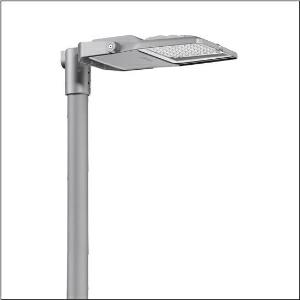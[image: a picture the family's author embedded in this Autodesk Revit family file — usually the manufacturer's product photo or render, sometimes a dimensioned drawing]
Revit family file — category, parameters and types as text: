
# Revit family: floodlight_fl_21_iq_mini___pl33t_5xa7772d2f3a_d038
name_source: partatom
category: Lighting Fixtures
units: mm (PartAtom-declared; Revit-internal decimal feet)

## family parameters
Cut with Voids When Loaded = No
Host = Face
Light Source = No
Part Type = Normal
Room Calculation Point = No
Round Connector Dimension = Use Diameter
Shared = No

## types (1)
- --- (1 x LED, 17620 lm, 143 W, 3000K)
    Apparent Load = 143 VA
    CIE Flux Codes = 26 75 99 100 100
    Color Rendering = 70
    Color Temperature = 3000K
    Default Elevation = 1800 mm
    Description = Floodlight FL 21 iQ mini, floodlight, primary light control with lens, of PMMA, primary optical cover: protective disc, of toughened safety glass, transparent, light distribution: PL33T, light emission: direct distribution, installation type: surface-mounted, LED, High Power LED, rated luminous flux: 17.620lm, luminous efficacy: 123lm/W, light colour: 730, colour temperature: 3000K, control: Auto-Match, Temp-Guard, Night-Set, Smart-Wire, Desk-Remote (wireless, voltage-free reading and setting of iQ features in the workshop via application-optimized NFC function/RFID function), optimised constant luminous flux control (CLO 2.0), Light-Fading, Lumen-Switch, with terminal, 6-pole, mains connection: 220..240V, AC, 50/60Hz, start of lifetime: 143W, end of service life: 152W, reduction: 61W, luminaire housing, of diecast aluminium, powder-coated, Siteco® metallic grey (DB 702S), corrosivity category C5 mid according to DIN EN ISO 12944, sealing non-destructively replaceable, please order mast flange separately, mast bracket, of steel, galvanised, powder-coated, protection rating (complete): IP66, insulation class (complete): insulation class II (safety insulation), certification: CE, ENEC, VDE, protection symbol: D, impact resistance: IK08, permissible operating ambient temperature: -40..+40°C, permissible operating ambient temperature for outdoor applications: -40..+50°C, standard: DIN EN 12944, LABS conformity tested according to VDMA 24364:2018-05, packaging unit: 1 piece

Light Distribution: PL33T
    Height = 70 mm
    Lamp = 1 x LED
    Lamp Light Flux = 17620 lm
    Lamp Power = 143 W
    Lamp count = 1
    Length = 485 mm
    Luminous efficacy = 123 lm/W
    Manufacturer = Siteco
    ModVariant = No
    Model = 5XA7772D2F3A
    Number of Poles = 1
    OnlyDefault = Yes
    Power Factor = 1
    Product Name = Floodlight FL 21 iQ mini | PL33T
    Product group = floodlight | pylon annexe
    ProductGroupID = 6200
    Protection Class = Protection class II
    Protection Degree = IP 66
    RLX_Detail_Level = 1
    RLX_Emergency_Light_Flux = 0 lm
    RLX_Emergency_Type = 0
    RLX_Emergency_Type_DB = No
    RlxData = <blob elided: 101397 chars, md5=4d4c4a81>
    Socket = socket
    Standby Power = 0 W
    System Light Flux = 17620 lm
    System Power = 143 W
    Type Comments = factory setting: luminous flux: 100 % | dim-lin: 254 | 730 mA
    Type Image = l_1007125.jpg
    URL = http://relux.com
    VarID = @adj_119265
    Voltage = 0 V
    Weight = 0.00 kg
    Width = 337 mm

## geometry (parser evidence)
native form markers: Blend x4, Sweep x12
no freeform markers — native parametric forms only
